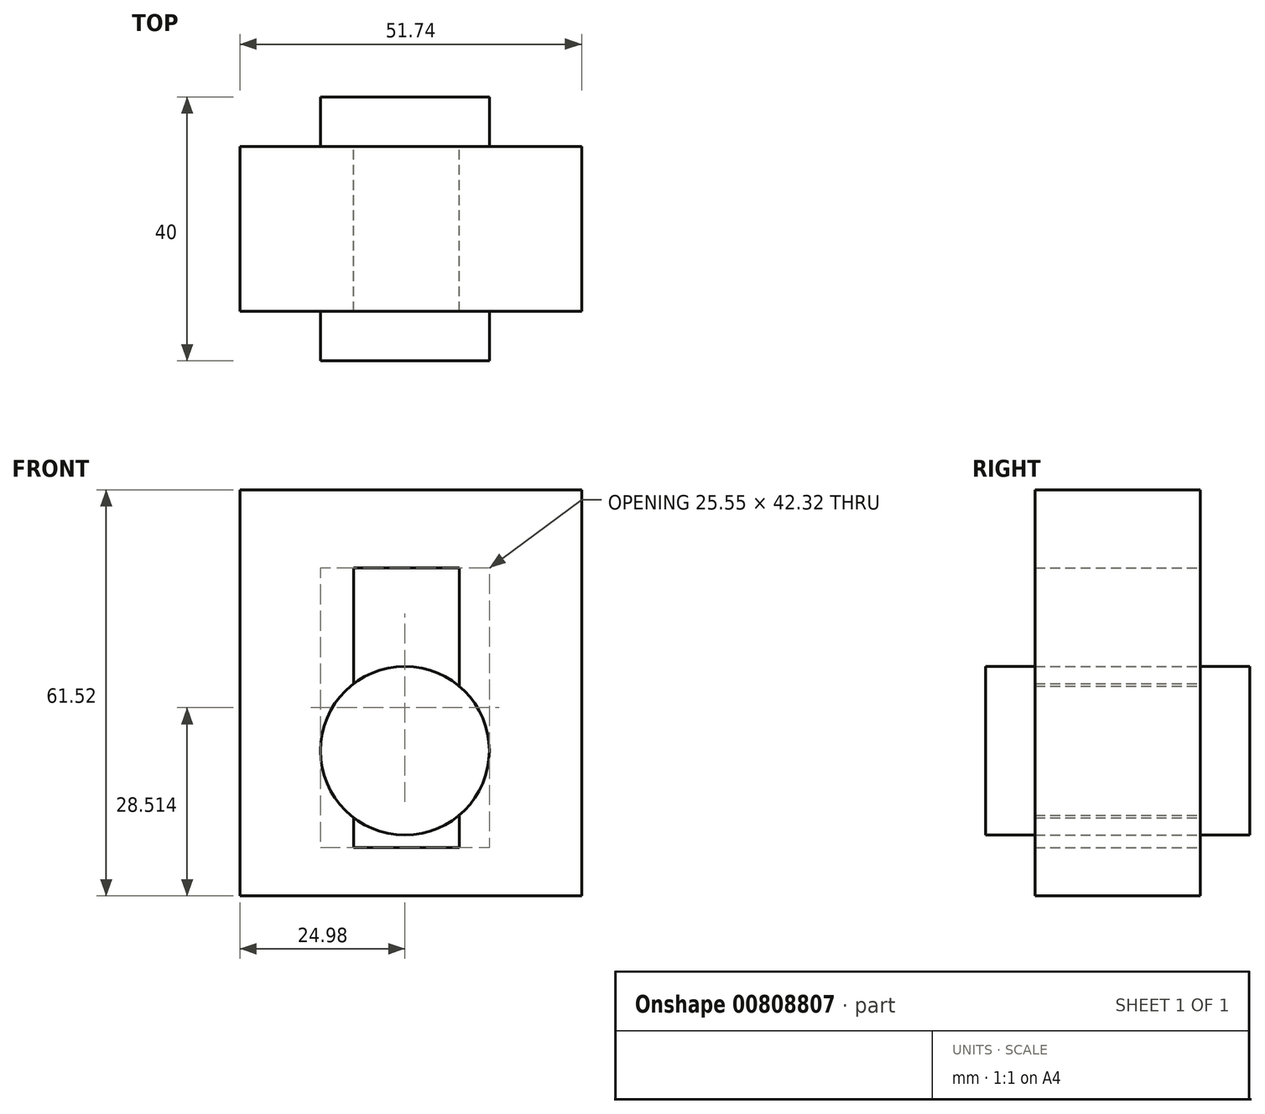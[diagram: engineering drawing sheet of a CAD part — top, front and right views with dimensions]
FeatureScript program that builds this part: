
annotation { "Feature Type Name" : "Feature", "Feature Type Description" : "" }
export const myFeature = defineFeature(function(context is Context, id is Id, definition is map)
    precondition{}
    {
        {
            var Q0;
            Q0=qCreatedBy(makeId("Front.planeOp"),FACE);
            var sketch = newSketch(context, id + "F0", { "sketchPlane" : qUnion([Q0])});
            skLineSegment(sketch, "E0.bottom", {"start": v(-24.98, 61.52) * mm, "end": v(26.76, 61.52) * mm});
            skLineSegment(sketch, "E0.top", {"start": v(-24.98, 0) * mm, "end": v(26.76, 0) * mm});
            skLineSegment(sketch, "E0.left", {"start": v(-24.98, 61.52) * mm, "end": v(-24.98, 0) * mm});
            skLineSegment(sketch, "E0.right", {"start": v(26.76, 61.52) * mm, "end": v(26.76, 0) * mm});
            skLineSegment(sketch, "E1.bottom", {"start": v(-7.74, 49.67) * mm, "end": v(8.24, 49.67) * mm});
            skLineSegment(sketch, "E1.top", {"start": v(-7.74, 7.36) * mm, "end": v(8.24, 7.36) * mm});
            skLineSegment(sketch, "E1.left", {"start": v(-7.74, 49.67) * mm, "end": v(-7.74, 7.36) * mm});
            skLineSegment(sketch, "E1.right", {"start": v(8.24, 49.67) * mm, "end": v(8.24, 7.36) * mm});
            skSolve(sketch);
        }
        {
            var Q0;
            Q0=makeQuery(id+"F0.imprint","IMPRINT",FACE,{"disambiguationData":[TD([[makeQuery(id+"F0.imprint","IMPRINT",EDGE,{"derivedFrom":sQuery(id+"F0.wireOp",EDGE,"E0.bottom")}),-1.0]])]});
            extrude(context, id + "F1", {"entities" : qUnion([Q0]), "endBound" : BoundingType.SYMMETRIC, "depth" : 25 * mm, "offsetDistance" : 25 * mm});
        }
        {
            var Q0;
            Q0=qCreatedBy(makeId("Front.planeOp"),FACE);
            var sketch = newSketch(context, id + "F2", { "sketchPlane" : qUnion([Q0])});
            skCircle(sketch, "E2", {"center": v(0, 22) * mm, "radius": 12.78 * mm});
            skSolve(sketch);
        }
        {
            var Q0;
            Q0=makeQuery(id+"F2.imprint","IMPRINT",FACE,{"disambiguationData":[TD([[makeQuery(id+"F2.imprint","IMPRINT",EDGE,{"derivedFrom":sQuery(id+"F2.wireOp",EDGE,"E2")}),1.0]])]});
            extrude(context, id + "F3", {"entities" : qUnion([Q0]), "operationType" : NewBodyOperationType.ADD, "endBound" : BoundingType.SYMMETRIC, "depth" : 40 * mm, "offsetDistance" : 25 * mm});
        }
    });
